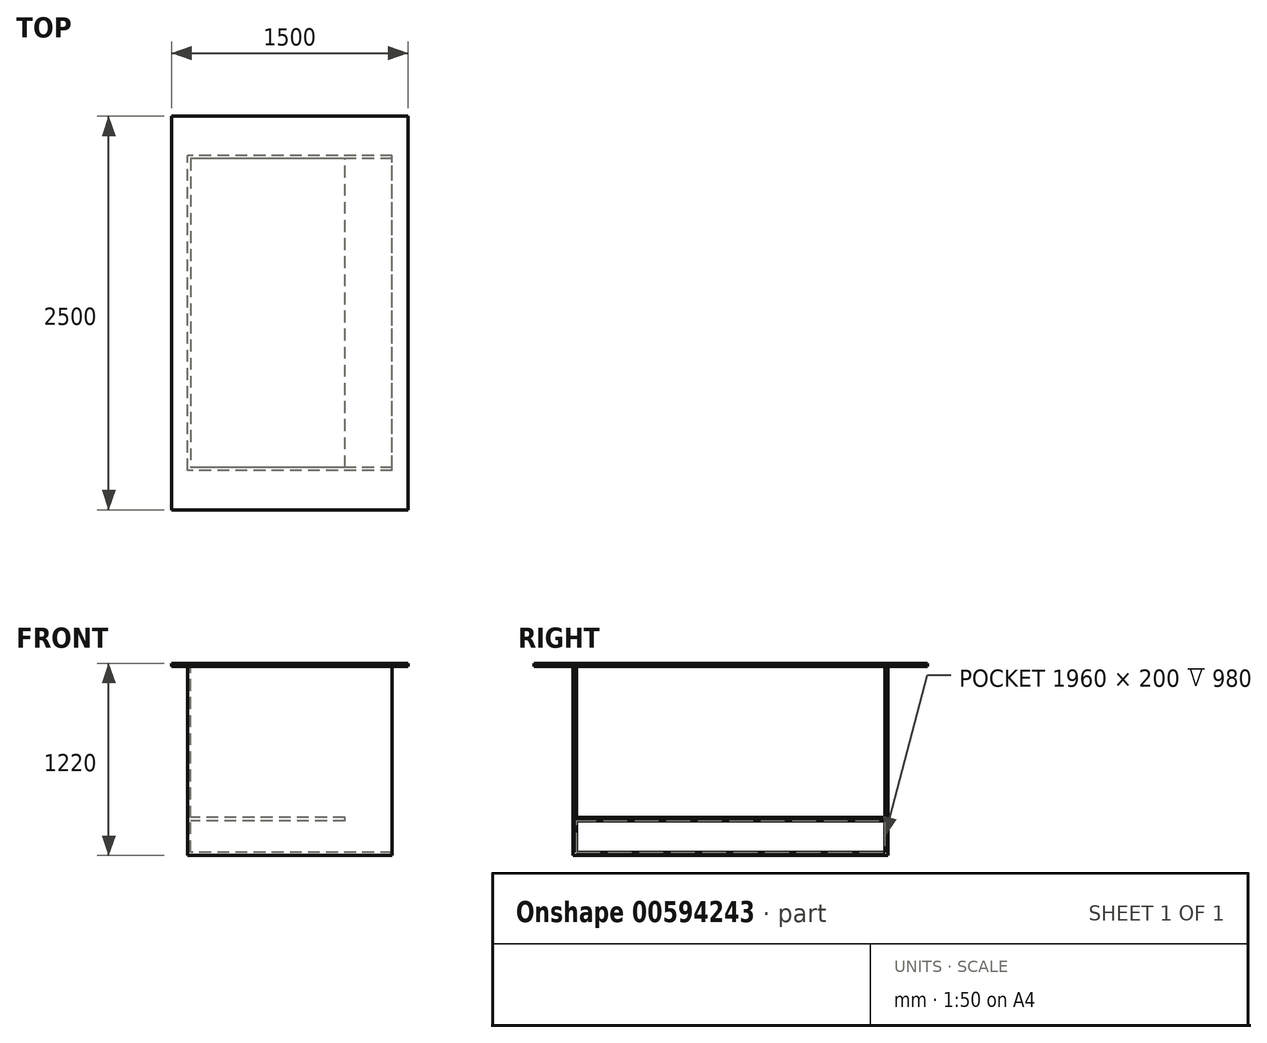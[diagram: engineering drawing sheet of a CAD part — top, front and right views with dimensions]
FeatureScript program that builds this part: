
annotation { "Feature Type Name" : "Feature", "Feature Type Description" : "" }
export const myFeature = defineFeature(function(context is Context, id is Id, definition is map)
    precondition{}
    {
        {
            var Q0;
            Q0=qCreatedBy(makeId("Right.planeOp"),FACE);
            var sketch = newSketch(context, id + "F0", { "sketchPlane" : qUnion([Q0])});
            skLineSegment(sketch, "E0.bottom", {"start": v(-1000, 0) * mm, "end": v(1000, 0) * mm});
            skLineSegment(sketch, "E0.top", {"start": v(-1000, 1200) * mm, "end": v(1000, 1200) * mm});
            skLineSegment(sketch, "E0.left", {"start": v(-1000, 0) * mm, "end": v(-1000, 1200) * mm});
            skLineSegment(sketch, "E0.right", {"start": v(1000, 0) * mm, "end": v(1000, 1200) * mm});
            skLineSegment(sketch, "E1.0", {"start": v(-980, 20) * mm, "end": v(-980, 1200) * mm});
            skLineSegment(sketch, "E1.1", {"start": v(-980, 20) * mm, "end": v(980, 20) * mm});
            skLineSegment(sketch, "E1.2", {"start": v(980, 20) * mm, "end": v(980, 1200) * mm});
            skLineSegment(sketch, "E2.bottom", {"start": v(-1250, 1220) * mm, "end": v(1250, 1220) * mm});
            skLineSegment(sketch, "E2.top", {"start": v(-1250, 1200) * mm, "end": v(1250, 1200) * mm});
            skLineSegment(sketch, "E2.left", {"start": v(-1250, 1220) * mm, "end": v(-1250, 1200) * mm});
            skLineSegment(sketch, "E2.right", {"start": v(1250, 1220) * mm, "end": v(1250, 1200) * mm});
            skPoint(sketch, "E3", {"position": v(0, 1220) * mm});
            skLineSegment(sketch, "E4.bottom", {"start": v(-980, 240) * mm, "end": v(980, 240) * mm});
            skLineSegment(sketch, "E4.top", {"start": v(-980, 220) * mm, "end": v(980, 220) * mm});
            skLineSegment(sketch, "E4.left", {"start": v(-980, 240) * mm, "end": v(-980, 220) * mm});
            skLineSegment(sketch, "E4.right", {"start": v(980, 240) * mm, "end": v(980, 220) * mm});
            skLineSegment(sketch, "E5.bottom", {"start": v(980, 220) * mm, "end": v(960, 220) * mm});
            skLineSegment(sketch, "E5.top", {"start": v(980, 20) * mm, "end": v(960, 20) * mm});
            skLineSegment(sketch, "E5.left", {"start": v(980, 220) * mm, "end": v(980, 20) * mm});
            skLineSegment(sketch, "E5.right", {"start": v(960, 220) * mm, "end": v(960, 20) * mm});
            skLineSegment(sketch, "E6.bottom", {"start": v(-980, 20) * mm, "end": v(-960, 20) * mm});
            skLineSegment(sketch, "E6.top", {"start": v(-980, 220) * mm, "end": v(-960, 220) * mm});
            skLineSegment(sketch, "E6.left", {"start": v(-980, 20) * mm, "end": v(-980, 220) * mm});
            skLineSegment(sketch, "E6.right", {"start": v(-960, 20) * mm, "end": v(-960, 220) * mm});
            skSolve(sketch);
        }
        {
            var Q0;
            Q0=qCreatedBy(makeId("Top.planeOp"),FACE);
            var sketch = newSketch(context, id + "F1", { "sketchPlane" : qUnion([Q0])});
            skLineSegment(sketch, "E7.bottom", {"start": v(0, -1000) * mm, "end": v(1300, -1000) * mm});
            skLineSegment(sketch, "E7.top", {"start": v(0, 1000) * mm, "end": v(1300, 1000) * mm});
            skLineSegment(sketch, "E7.left", {"start": v(0, -1000) * mm, "end": v(0, 1000) * mm});
            skLineSegment(sketch, "E7.right", {"start": v(1300, -1000) * mm, "end": v(1300, 1000) * mm});
            skLineSegment(sketch, "E8", {"start": v(1000, 1000) * mm, "end": v(1000, -1000) * mm});
            skLineSegment(sketch, "E9.bottom", {"start": v(1300, 1000) * mm, "end": v(1400, 1000) * mm});
            skLineSegment(sketch, "E9.top", {"start": v(1300, -1000) * mm, "end": v(1400, -1000) * mm});
            skLineSegment(sketch, "E9.left", {"start": v(1300, 1000) * mm, "end": v(1300, -1000) * mm});
            skLineSegment(sketch, "E9.right", {"start": v(1400, 1000) * mm, "end": v(1400, -1000) * mm});
            skLineSegment(sketch, "E10", {"start": v(20, 1000) * mm, "end": v(20, -1000) * mm});
            skLineSegment(sketch, "E11.bottom", {"start": v(0, 1000) * mm, "end": v(-100, 1000) * mm});
            skLineSegment(sketch, "E11.top", {"start": v(0, -1000) * mm, "end": v(-100, -1000) * mm});
            skLineSegment(sketch, "E11.left", {"start": v(0, 1000) * mm, "end": v(0, -1000) * mm});
            skLineSegment(sketch, "E11.right", {"start": v(-100, 1000) * mm, "end": v(-100, -1000) * mm});
            skSolve(sketch);
        }
        {
            var Q0;
            Q0=makeQuery(id+"F0.imprint","IMPRINT",FACE,{"disambiguationData":[TD([[makeQuery(id+"F0.imprint","IMPRINT",EDGE,{"derivedFrom":sQuery(id+"F0.wireOp",EDGE,"E0.bottom")}),1.0]])]});
            var Q1;
            Q1=sQuery(id+"F1.wireOp",VERTEX,"E9.top.start");
            extrude(context, id + "F2", {"entities" : qUnion([Q0]), "endBound" : BoundingType.UP_TO_VERTEX, "depth" : 25 * mm, "endBoundEntityVertex" : qUnion([Q1]), "offsetDistance" : 25 * mm});
        }
        {
            var Q0;
            Q0=makeQuery(id+"F0.imprint","IMPRINT",FACE,{"disambiguationData":[TD([[makeQuery(id+"F0.imprint","IMPRINT",EDGE,{"derivedFrom":sQuery(id+"F0.wireOp",EDGE,"E1.1")}),1.0]])]});
            var Q1;
            {var subQ0=sQuery(id+"F0.wireOp",EDGE,"E1.0");Q1=makeQuery(id+"F0.imprint","IMPRINT",FACE,{"disambiguationData":[TD([[makeQuery(id+"F0.imprint","IMPRINT",EDGE,{"derivedFrom":subQ0}),-1.0]])]});}
            var Q2;
            Q2=makeQuery(id+"F0.imprint","IMPRINT",FACE,{"disambiguationData":[TD([[makeQuery(id+"F0.imprint","IMPRINT",EDGE,{"derivedFrom":sQuery(id+"F0.wireOp",EDGE,"E4.bottom")}),-1.0]])]});
            var Q3;
            Q3=makeQuery(id+"F0.imprint","IMPRINT",FACE,{"disambiguationData":[TD([[makeQuery(id+"F0.imprint","IMPRINT",EDGE,{"derivedFrom":sQuery(id+"F0.wireOp",EDGE,"E5.bottom")}),1.0]])]});
            var Q4;
            Q4=makeQuery(id+"F0.imprint","IMPRINT",FACE,{"disambiguationData":[TD([[makeQuery(id+"F0.imprint","IMPRINT",EDGE,{"derivedFrom":sQuery(id+"F0.wireOp",EDGE,"E6.bottom")}),1.0]])]});
            var Q5;
            Q5=sQuery(id+"F1.wireOp",VERTEX,"E10.end");
            extrude(context, id + "F3", {"entities" : qUnion([Q0, Q1, Q2, Q3, Q4]), "operationType" : NewBodyOperationType.ADD, "endBound" : BoundingType.UP_TO_VERTEX, "depth" : 25 * mm, "endBoundEntityVertex" : qUnion([Q5]), "offsetDistance" : 25 * mm});
        }
        {
            var Q0;
            Q0=makeQuery(id+"F0.imprint","IMPRINT",FACE,{"disambiguationData":[TD([[makeQuery(id+"F0.imprint","IMPRINT",EDGE,{"derivedFrom":sQuery(id+"F0.wireOp",EDGE,"E6.bottom")}),1.0]])]});
            var Q1;
            Q1=makeQuery(id+"F0.imprint","IMPRINT",FACE,{"disambiguationData":[TD([[makeQuery(id+"F0.imprint","IMPRINT",EDGE,{"derivedFrom":sQuery(id+"F0.wireOp",EDGE,"E4.bottom")}),-1.0]])]});
            var Q2;
            Q2=makeQuery(id+"F0.imprint","IMPRINT",FACE,{"disambiguationData":[TD([[makeQuery(id+"F0.imprint","IMPRINT",EDGE,{"derivedFrom":sQuery(id+"F0.wireOp",EDGE,"E5.bottom")}),1.0]])]});
            var Q3;
            Q3=sQuery(id+"F1.wireOp",VERTEX,"E8.end");
            extrude(context, id + "F4", {"entities" : qUnion([Q0, Q1, Q2]), "operationType" : NewBodyOperationType.ADD, "endBound" : BoundingType.UP_TO_VERTEX, "depth" : 25 * mm, "endBoundEntityVertex" : qUnion([Q3]), "offsetDistance" : 25 * mm});
        }
        {
            var Q0;
            Q0=makeQuery(id+"F0.imprint","IMPRINT",FACE,{"disambiguationData":[TD([[makeQuery(id+"F0.imprint","IMPRINT",EDGE,{"derivedFrom":sQuery(id+"F0.wireOp",EDGE,"E2.bottom")}),-1.0]])]});
            var Q1;
            Q1=sQuery(id+"F1.wireOp",VERTEX,"E9.top.end");
            var Q2;
            Q2=sQuery(id+"F1.wireOp",VERTEX,"E11.top.end");
            extrude(context, id + "F5", {"entities" : qUnion([Q0]), "operationType" : NewBodyOperationType.ADD, "endBound" : BoundingType.UP_TO_VERTEX, "depth" : 25 * mm, "endBoundEntityVertex" : qUnion([Q1]), "offsetDistance" : 25 * mm, "hasSecondDirection" : true, "secondDirectionBound" : SecondDirectionBoundingType.UP_TO_VERTEX, "secondDirectionOppositeDirection" : true, "secondDirectionDepth" : 25 * mm, "secondDirectionBoundEntityVertex" : qUnion([Q2])});
        }
    });
